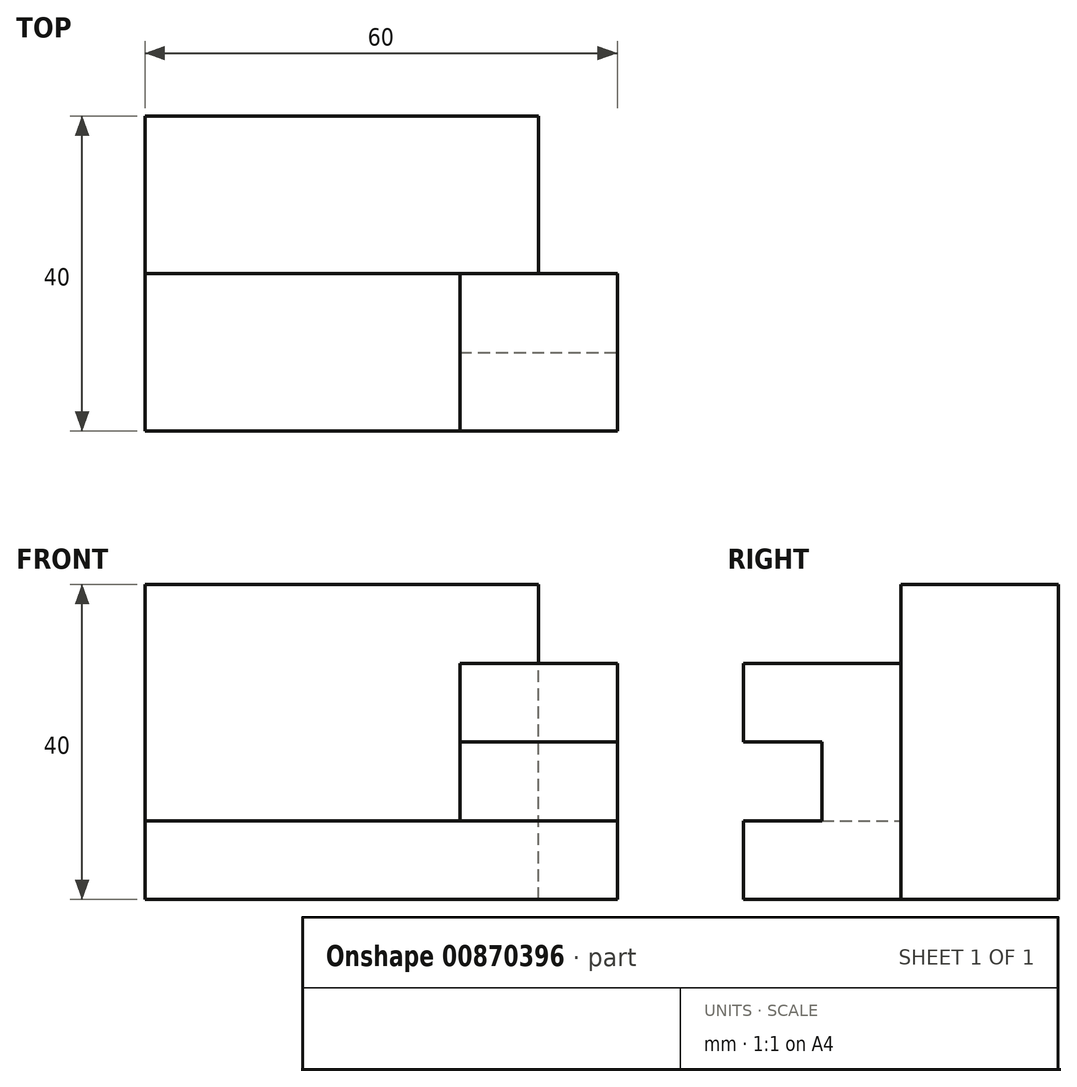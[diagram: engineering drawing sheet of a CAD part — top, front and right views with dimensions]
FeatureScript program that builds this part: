
annotation { "Feature Type Name" : "Feature", "Feature Type Description" : "" }
export const myFeature = defineFeature(function(context is Context, id is Id, definition is map)
    precondition{}
    {
        {
            var Q0;
            Q0=qCreatedBy(makeId("Top.planeOp"),FACE);
            var sketch = newSketch(context, id + "F0", { "sketchPlane" : qUnion([Q0])});
            skLineSegment(sketch, "E0.bottom", {"start": v(0, 0) * mm, "end": v(60, 0) * mm});
            skLineSegment(sketch, "E0.top", {"start": v(0, 20) * mm, "end": v(60, 20) * mm});
            skLineSegment(sketch, "E0.left", {"start": v(0, 0) * mm, "end": v(0, 20) * mm});
            skLineSegment(sketch, "E0.right", {"start": v(60, 0) * mm, "end": v(60, 20) * mm});
            skLineSegment(sketch, "E1.bottom", {"start": v(0, 20) * mm, "end": v(50, 20) * mm});
            skLineSegment(sketch, "E1.top", {"start": v(0, 40) * mm, "end": v(50, 40) * mm});
            skLineSegment(sketch, "E1.left", {"start": v(0, 20) * mm, "end": v(0, 40) * mm});
            skLineSegment(sketch, "E1.right", {"start": v(50, 20) * mm, "end": v(50, 40) * mm});
            skLineSegment(sketch, "E2.bottom", {"start": v(60, 0) * mm, "end": v(40, 0) * mm});
            skLineSegment(sketch, "E2.top", {"start": v(60, 20) * mm, "end": v(40, 20) * mm});
            skLineSegment(sketch, "E2.right", {"start": v(40, 0) * mm, "end": v(40, 20) * mm});
            skLineSegment(sketch, "E3", {"start": v(60, 10) * mm, "end": v(40, 10) * mm, "construction": true});
            skSolve(sketch);
        }
        {
            var Q0;
            Q0=makeQuery(id+"F0.imprint","IMPRINT",FACE,{"disambiguationData":[TD([[makeQuery(id+"F0.imprint","IMPRINT",EDGE,{"derivedFrom":sQuery(id+"F0.wireOp",EDGE,"E1.top")}),-1.0]])]});
            var Q1;
            {var subQ0=sQuery(id+"F0.wireOp",EDGE,"E0.left");Q1=makeQuery(id+"F0.imprint","IMPRINT",FACE,{"disambiguationData":[TD([[makeQuery(id+"F0.imprint","IMPRINT",EDGE,{"derivedFrom":subQ0}),-1.0]])]});}
            var Q2;
            {var subQ0=sQuery(id+"F0.wireOp",EDGE,"E0.right");Q2=makeQuery(id+"F0.imprint","IMPRINT",FACE,{"disambiguationData":[TD([[makeQuery(id+"F0.imprint","IMPRINT",EDGE,{"derivedFrom":subQ0}),1.0]])]});}
            extrude(context, id + "F1", {"entities" : qUnion([Q0, Q1, Q2]), "oppositeDirection" : true, "depth" : 10 * mm, "offsetDistance" : 25 * mm});
        }
        {
            var Q0;
            Q0=makeQuery(id+"F0.imprint","IMPRINT",FACE,{"disambiguationData":[TD([[makeQuery(id+"F0.imprint","IMPRINT",EDGE,{"derivedFrom":sQuery(id+"F0.wireOp",EDGE,"E1.top")}),-1.0]])]});
            extrude(context, id + "F2", {"entities" : qUnion([Q0]), "operationType" : NewBodyOperationType.ADD, "depth" : 30 * mm, "offsetDistance" : 25 * mm});
        }
        {
            var Q0;
            {var subQ0=sQuery(id+"F0.wireOp",EDGE,"E0.right");Q0=makeQuery(id+"F0.imprint","IMPRINT",FACE,{"disambiguationData":[TD([[makeQuery(id+"F0.imprint","IMPRINT",EDGE,{"derivedFrom":subQ0}),1.0]])]});}
            extrude(context, id + "F3", {"entities" : qUnion([Q0]), "operationType" : NewBodyOperationType.ADD, "depth" : 20 * mm, "offsetDistance" : 25 * mm});
        }
        {
            var Q0;
            {var subQ0=sQuery(id+"F0.wireOp",EDGE,"E0.right");Q0=makeQuery(id+"F3.boolean.opBoolean","MERGE",FACE,{"derivedFrom":[makeQuery(id+"F1.opExtrude","SWEPT_FACE",FACE,{"disambiguationData":[OSD([subQ0])]}),makeQuery(id+"F3.opExtrude","SWEPT_FACE",FACE,{"disambiguationData":[OSD([subQ0])]})]});}
            var sketch = newSketch(context, id + "F4", { "sketchPlane" : qUnion([Q0])});
            skLineSegment(sketch, "E4", {"start": v(0, 0) * mm, "end": v(20, 0) * mm});
            skLineSegment(sketch, "E5", {"start": v(0, 10) * mm, "end": v(20, 10) * mm});
            skLineSegment(sketch, "E6", {"start": v(0, 0) * mm, "end": v(0, 10) * mm});
            skLineSegment(sketch, "E7", {"start": v(20, 0) * mm, "end": v(20, 10) * mm});
            skLineSegment(sketch, "E8", {"start": v(10, 10) * mm, "end": v(10, 0) * mm});
            skSolve(sketch);
        }
        {
            var Q0;
            {var subQ0=sQuery(id+"F4.wireOp",EDGE,"E6");Q0=makeQuery(id+"F4.imprint","IMPRINT",FACE,{"disambiguationData":[TD([[makeQuery(id+"F4.imprint","IMPRINT",EDGE,{"derivedFrom":subQ0}),-1.0]])]});}
            extrude(context, id + "F5", {"entities" : qUnion([Q0]), "operationType" : NewBodyOperationType.REMOVE, "oppositeDirection" : true, "depth" : 25 * mm, "offsetDistance" : 25 * mm});
        }
    });
